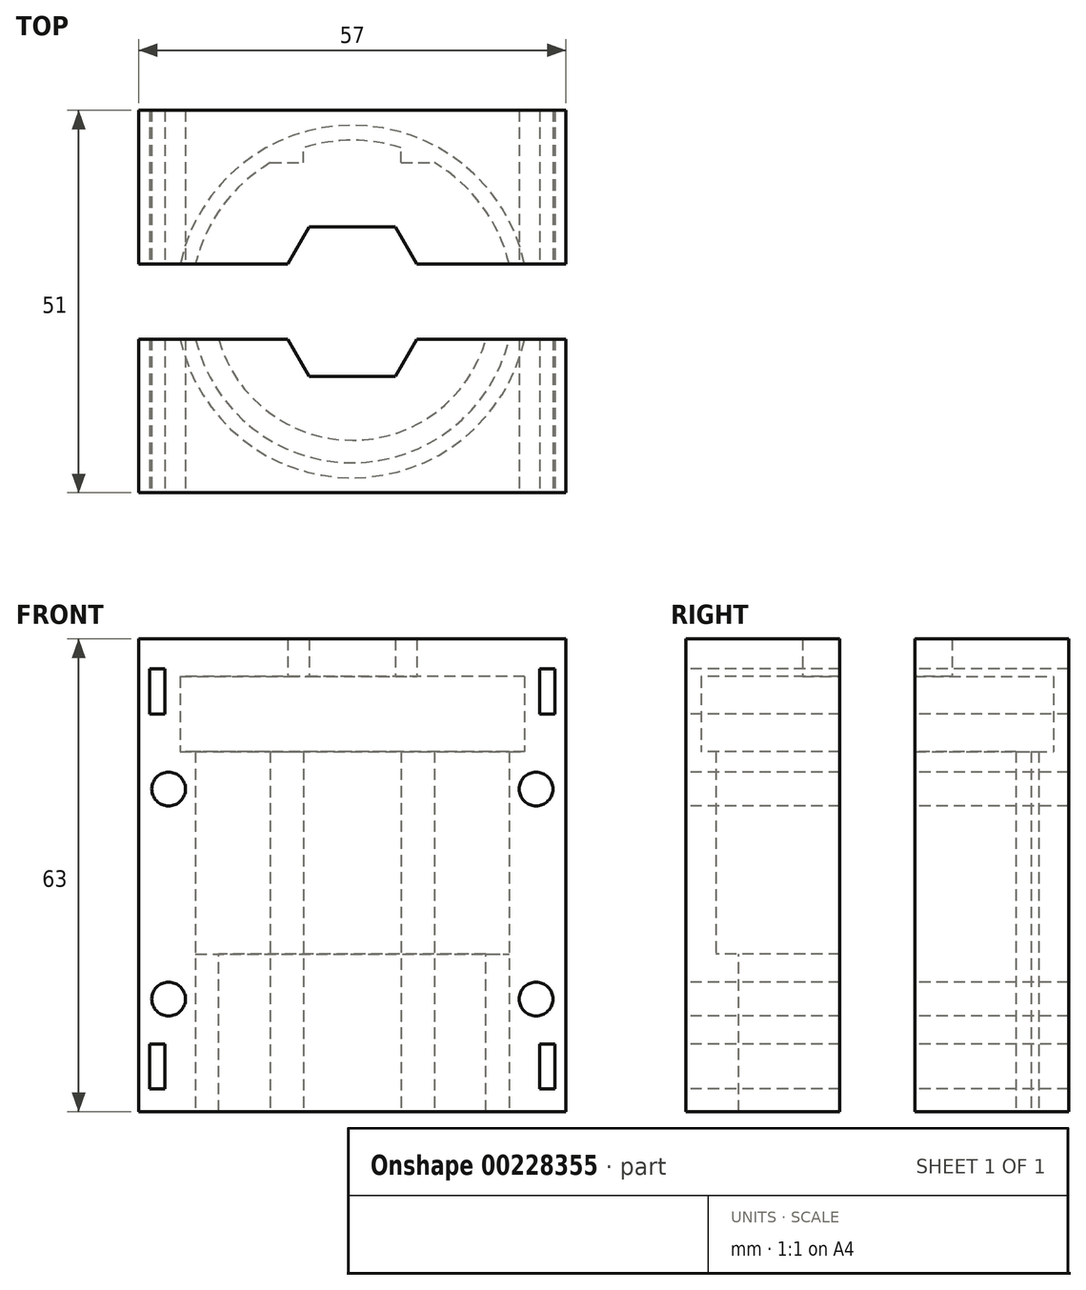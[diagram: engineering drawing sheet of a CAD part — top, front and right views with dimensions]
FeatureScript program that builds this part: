
annotation { "Feature Type Name" : "Feature", "Feature Type Description" : "" }
export const myFeature = defineFeature(function(context is Context, id is Id, definition is map)
    precondition{}
    {
        {
            var Q0;
            Q0=qCreatedBy(makeId("Top.planeOp"),FACE);
            var sketch = newSketch(context, id + "F0", { "sketchPlane" : qUnion([Q0])});
            skArc(sketch, "E0", {"start": v(-10.54, 17) * mm, "mid": v(0, -20) * mm, "end": v(10.54, 17) * mm, "construction": true});
            skLineSegment(sketch, "E1", {"start": v(0, 0) * mm, "end": v(0, 20) * mm, "construction": true});
            skLineSegment(sketch, "E2.0", {"start": v(5, 17) * mm, "end": v(5, 19.36) * mm, "construction": true});
            skLineSegment(sketch, "E3.0", {"start": v(-5, 17) * mm, "end": v(-5, 19.36) * mm, "construction": true});
            skLineSegment(sketch, "E4", {"start": v(-10.54, 17) * mm, "end": v(-5, 17) * mm, "construction": true});
            skLineSegment(sketch, "E5.trimOffspring", {"start": v(5, 17) * mm, "end": v(10.54, 17) * mm, "construction": true});
            skArc(sketch, "E6.trimOffspring", {"start": v(5, 19.36) * mm, "mid": v(0, 20) * mm, "end": v(-5, 19.36) * mm, "construction": true});
            skLineSegment(sketch, "E7.0", {"start": v(6.5, 18.5) * mm, "end": v(6.5, 20.5) * mm});
            skLineSegment(sketch, "E7.1", {"start": v(-6.5, 18.5) * mm, "end": v(-6.5, 20.5) * mm});
            skLineSegment(sketch, "E7.2", {"start": v(-10.95, 18.5) * mm, "end": v(-6.5, 18.5) * mm});
            skArc(sketch, "E7.3", {"start": v(6.5, 20.5) * mm, "mid": v(0, 21.5) * mm, "end": v(-6.5, 20.5) * mm});
            skArc(sketch, "E7.4", {"start": v(-10.95, 18.5) * mm, "mid": v(-18.68, 10.65) * mm, "end": v(-21.5, 0) * mm});
            skLineSegment(sketch, "E7.5", {"start": v(6.5, 18.5) * mm, "end": v(10.95, 18.5) * mm});
            skLineSegment(sketch, "E8", {"start": v(-21.5, 0) * mm, "end": v(21.5, 0) * mm, "construction": true});
            skLineSegment(sketch, "E9", {"start": v(-21.5, 21.5) * mm, "end": v(-21.5, -21.5) * mm, "construction": true});
            skLineSegment(sketch, "E10", {"start": v(21.5, 21.5) * mm, "end": v(21.5, -21.5) * mm, "construction": true});
            skLineSegment(sketch, "E11", {"start": v(-21.5, 21.5) * mm, "end": v(21.5, 21.5) * mm, "construction": true});
            skPoint(sketch, "E11.startSnap0", {"position": v(0, 21.5) * mm});
            skLineSegment(sketch, "E12", {"start": v(-21.5, -21.5) * mm, "end": v(21.5, -21.5) * mm, "construction": true});
            skPoint(sketch, "E12.startSnap0", {"position": v(0, -21.5) * mm});
            skLineSegment(sketch, "E13.0", {"start": v(-28.5, 25.5) * mm, "end": v(-28.5, 5) * mm});
            skLineSegment(sketch, "E14.0", {"start": v(28.5, 25.5) * mm, "end": v(28.5, 5) * mm});
            skLineSegment(sketch, "E15.0", {"start": v(-28.5, 25.5) * mm, "end": v(28.5, 25.5) * mm});
            skLineSegment(sketch, "E16.0", {"start": v(-28.5, -25.5) * mm, "end": v(28.5, -25.5) * mm});
            skLineSegment(sketch, "E17.0", {"start": v(-28.5, -5) * mm, "end": v(-20.91, -5) * mm});
            skLineSegment(sketch, "E18.0", {"start": v(-28.5, 5) * mm, "end": v(-20.91, 5) * mm});
            skLineSegment(sketch, "E19.trimOffspring", {"start": v(-28.5, -5) * mm, "end": v(-28.5, -25.5) * mm});
            skLineSegment(sketch, "E20.trimOffspring", {"start": v(28.5, -5) * mm, "end": v(28.5, -25.5) * mm});
            skArc(sketch, "E21.trimOffspring", {"start": v(20.91, 5) * mm, "mid": v(17.3, 12.76) * mm, "end": v(10.95, 18.5) * mm});
            skArc(sketch, "E22.trimOffspring", {"start": v(-20.91, -5) * mm, "mid": v(0, -21.5) * mm, "end": v(20.91, -5) * mm});
            skLineSegment(sketch, "E23.trimOffspring", {"start": v(20.91, -5) * mm, "end": v(28.5, -5) * mm});
            skLineSegment(sketch, "E24.trimOffspring", {"start": v(20.91, 5) * mm, "end": v(28.5, 5) * mm});
            skSolve(sketch);
        }
        {
            var Q0;
            Q0=makeQuery(id+"F0.imprint","IMPRINT",FACE,{"disambiguationData":[TD([[makeQuery(id+"F0.imprint","IMPRINT",EDGE,{"derivedFrom":sQuery(id+"F0.wireOp",EDGE,"E7.0")}),-1.0]])]});
            var Q1;
            Q1=makeQuery(id+"F0.imprint","IMPRINT",FACE,{"disambiguationData":[TD([[makeQuery(id+"F0.imprint","IMPRINT",EDGE,{"derivedFrom":sQuery(id+"F0.wireOp",EDGE,"E16.0")}),1.0]])]});
            extrude(context, id + "F1", {"entities" : qUnion([Q0, Q1]), "depth" : 27 * mm});
        }
        {
            var Q0;
            Q0=makeQuery(id+"F1.opExtrude","CAP_FACE",FACE,{"disambiguationData":[OSD([sQuery(id+"F0.wireOp",EDGE,"E7.0"),sQuery(id+"F0.wireOp",EDGE,"E7.1"),sQuery(id+"F0.wireOp",EDGE,"E7.2"),sQuery(id+"F0.wireOp",EDGE,"E7.3"),sQuery(id+"F0.wireOp",EDGE,"E7.4"),sQuery(id+"F0.wireOp",EDGE,"E7.5"),sQuery(id+"F0.wireOp",EDGE,"E13.0"),sQuery(id+"F0.wireOp",EDGE,"E14.0"),sQuery(id+"F0.wireOp",EDGE,"E15.0"),sQuery(id+"F0.wireOp",EDGE,"E18.0"),sQuery(id+"F0.wireOp",EDGE,"E21.trimOffspring"),sQuery(id+"F0.wireOp",EDGE,"E24.trimOffspring")])],"isStart":false});
            var sketch = newSketch(context, id + "F2", { "sketchPlane" : qUnion([Q0])});
            skLineSegment(sketch, "E25.0.0", {"start": v(28.5, 25.5) * mm, "end": v(-28.5, 25.5) * mm});
            skLineSegment(sketch, "E25.0.1", {"start": v(-28.5, 25.5) * mm, "end": v(-28.5, 5) * mm});
            skLineSegment(sketch, "E25.0.2", {"start": v(-28.5, 5) * mm, "end": v(-22.96, 5) * mm});
            skArc(sketch, "E25.0.3", {"start": v(-20.91, 5) * mm, "mid": v(-17.3, 12.76) * mm, "end": v(-10.95, 18.5) * mm, "construction": true});
            skLineSegment(sketch, "E25.0.4", {"start": v(-10.95, 18.5) * mm, "end": v(-6.5, 18.5) * mm, "construction": true});
            skLineSegment(sketch, "E25.0.5", {"start": v(-6.5, 18.5) * mm, "end": v(-6.5, 20.5) * mm, "construction": true});
            skArc(sketch, "E25.0.6", {"start": v(-6.5, 20.5) * mm, "mid": v(0, 21.5) * mm, "end": v(6.5, 20.5) * mm, "construction": true});
            skLineSegment(sketch, "E25.0.7", {"start": v(6.5, 20.5) * mm, "end": v(6.5, 18.5) * mm, "construction": true});
            skLineSegment(sketch, "E25.0.8", {"start": v(6.5, 18.5) * mm, "end": v(10.95, 18.5) * mm, "construction": true});
            skArc(sketch, "E25.0.9", {"start": v(10.95, 18.5) * mm, "mid": v(17.3, 12.76) * mm, "end": v(20.91, 5) * mm, "construction": true});
            skLineSegment(sketch, "E25.0.10", {"start": v(20.91, 5) * mm, "end": v(22.96, 5) * mm, "construction": true});
            skLineSegment(sketch, "E25.0.11", {"start": v(28.5, 5) * mm, "end": v(28.5, 25.5) * mm});
            skArc(sketch, "E26.0.0", {"start": v(20.91, -5) * mm, "mid": v(0, -21.5) * mm, "end": v(-20.91, -5) * mm, "construction": true});
            skLineSegment(sketch, "E26.0.1", {"start": v(-20.91, -5) * mm, "end": v(-22.96, -5) * mm, "construction": true});
            skLineSegment(sketch, "E26.0.2", {"start": v(-28.5, -5) * mm, "end": v(-28.5, -25.5) * mm});
            skLineSegment(sketch, "E26.0.3", {"start": v(-28.5, -25.5) * mm, "end": v(28.5, -25.5) * mm});
            skLineSegment(sketch, "E26.0.4", {"start": v(28.5, -25.5) * mm, "end": v(28.5, -5) * mm});
            skLineSegment(sketch, "E26.0.5", {"start": v(28.5, -5) * mm, "end": v(22.96, -5) * mm});
            skArc(sketch, "E27.0", {"start": v(22.96, -5) * mm, "mid": v(0, -23.5) * mm, "end": v(-22.96, -5) * mm});
            skLineSegment(sketch, "E28", {"start": v(-22.96, -5) * mm, "end": v(-28.5, -5) * mm});
            skLineSegment(sketch, "E29", {"start": v(22.96, -5) * mm, "end": v(20.91, -5) * mm, "construction": true});
            skArc(sketch, "E30.0", {"start": v(-22.96, 5) * mm, "mid": v(0, 23.5) * mm, "end": v(22.96, 5) * mm});
            skLineSegment(sketch, "E31", {"start": v(-22.96, 5) * mm, "end": v(-20.91, 5) * mm, "construction": true});
            skLineSegment(sketch, "E32", {"start": v(22.96, 5) * mm, "end": v(28.5, 5) * mm});
            skSolve(sketch);
        }
        {
            var Q0;
            Q0=makeQuery(id+"F2.imprint","IMPRINT",FACE,{"disambiguationData":[TD([[makeQuery(id+"F2.imprint","IMPRINT",EDGE,{"derivedFrom":sQuery(id+"F2.wireOp",EDGE,"E25.0.0")}),-1.0]])]});
            extrude(context, id + "F3", {"entities" : qUnion([Q0]), "operationType" : NewBodyOperationType.ADD, "depth" : 10 * mm});
        }
        {
            var Q0;
            Q0=makeQuery(id+"F2.imprint","IMPRINT",FACE,{"disambiguationData":[TD([[makeQuery(id+"F2.imprint","IMPRINT",EDGE,{"derivedFrom":sQuery(id+"F2.wireOp",EDGE,"E26.0.2")}),1.0]])]});
            extrude(context, id + "F4", {"entities" : qUnion([Q0]), "operationType" : NewBodyOperationType.ADD, "depth" : 10 * mm});
        }
        {
            var Q0;
            Q0=makeQuery(id+"F3.opExtrude","CAP_FACE",FACE,{"disambiguationData":[OSD([sQuery(id+"F2.wireOp",EDGE,"E25.0.0"),sQuery(id+"F2.wireOp",EDGE,"E25.0.1"),sQuery(id+"F2.wireOp",EDGE,"E25.0.2"),sQuery(id+"F2.wireOp",EDGE,"E25.0.11"),sQuery(id+"F2.wireOp",EDGE,"E30.0"),sQuery(id+"F2.wireOp",EDGE,"E32")])],"isStart":false});
            var sketch = newSketch(context, id + "F5", { "sketchPlane" : qUnion([Q0])});
            skLineSegment(sketch, "E33.0.0", {"start": v(-28.5, 5) * mm, "end": v(-22.96, 5) * mm});
            skLineSegment(sketch, "E33.0.2", {"start": v(22.96, 5) * mm, "end": v(28.5, 5) * mm});
            skLineSegment(sketch, "E33.0.3", {"start": v(28.5, 5) * mm, "end": v(28.5, 25.5) * mm});
            skLineSegment(sketch, "E33.0.4", {"start": v(28.5, 25.5) * mm, "end": v(-28.5, 25.5) * mm});
            skLineSegment(sketch, "E33.0.5", {"start": v(-28.5, 25.5) * mm, "end": v(-28.5, 5) * mm});
            skLineSegment(sketch, "E34.0.1", {"start": v(-22.96, -5) * mm, "end": v(-28.5, -5) * mm});
            skLineSegment(sketch, "E34.0.2", {"start": v(-28.5, -5) * mm, "end": v(-28.5, -25.5) * mm});
            skLineSegment(sketch, "E34.0.3", {"start": v(-28.5, -25.5) * mm, "end": v(28.5, -25.5) * mm});
            skLineSegment(sketch, "E34.0.4", {"start": v(28.5, -25.5) * mm, "end": v(28.5, -5) * mm});
            skLineSegment(sketch, "E34.0.5", {"start": v(28.5, -5) * mm, "end": v(22.96, -5) * mm});
            skLineSegment(sketch, "E35", {"start": v(0, 0) * mm, "end": v(28.5, 0) * mm, "construction": true});
            skCircle(sketch, "E36.cCircle", {"center": v(0, 0) * mm, "radius": 11.5 * mm, "construction": true});
            skLineSegment(sketch, "E36.0", {"start": v(8.61, -5) * mm, "end": v(5.75, -9.96) * mm});
            skLineSegment(sketch, "E36.1", {"start": v(5.75, -9.96) * mm, "end": v(-5.75, -9.96) * mm});
            skLineSegment(sketch, "E36.2", {"start": v(-5.75, -9.96) * mm, "end": v(-8.61, -5) * mm});
            skLineSegment(sketch, "E36.3", {"start": v(-8.61, 5) * mm, "end": v(-5.75, 9.96) * mm});
            skLineSegment(sketch, "E36.4", {"start": v(-5.75, 9.96) * mm, "end": v(5.75, 9.96) * mm});
            skLineSegment(sketch, "E36.5", {"start": v(5.75, 9.96) * mm, "end": v(8.61, 5) * mm});
            skLineSegment(sketch, "E37", {"start": v(-22.96, 5) * mm, "end": v(-8.61, 5) * mm});
            skLineSegment(sketch, "E38", {"start": v(22.96, 5) * mm, "end": v(8.61, 5) * mm});
            skLineSegment(sketch, "E39", {"start": v(-22.96, -5) * mm, "end": v(-8.61, -5) * mm});
            skLineSegment(sketch, "E40", {"start": v(22.96, -5) * mm, "end": v(8.61, -5) * mm});
            skPoint(sketch, "E41.orphan", {"position": v(11.5, 0) * mm});
            skPoint(sketch, "E42.orphan", {"position": v(-11.5, 0) * mm});
            skSolve(sketch);
        }
        {
            var Q0;
            Q0=makeQuery(id+"F5.imprint","IMPRINT",FACE,{"disambiguationData":[TD([[makeQuery(id+"F5.imprint","IMPRINT",EDGE,{"derivedFrom":sQuery(id+"F5.wireOp",EDGE,"E36.3")}),1.0]])]});
            var Q1;
            Q1=makeQuery(id+"F5.imprint","IMPRINT",FACE,{"disambiguationData":[TD([[makeQuery(id+"F5.imprint","IMPRINT",EDGE,{"derivedFrom":sQuery(id+"F5.wireOp",EDGE,"E33.0.0")}),1.0]])]});
            extrude(context, id + "F6", {"entities" : qUnion([Q0, Q1]), "operationType" : NewBodyOperationType.ADD, "depth" : 5 * mm});
        }
        {
            var Q0;
            Q0=makeQuery(id+"F5.imprint","IMPRINT",FACE,{"disambiguationData":[TD([[makeQuery(id+"F5.imprint","IMPRINT",EDGE,{"derivedFrom":sQuery(id+"F5.wireOp",EDGE,"E34.0.1")}),1.0]])]});
            extrude(context, id + "F7", {"entities" : qUnion([Q0]), "operationType" : NewBodyOperationType.ADD, "depth" : 5 * mm});
        }
        {
            var Q0;
            Q0=makeQuery(id+"F1.opExtrude","CAP_FACE",FACE,{"disambiguationData":[OSD([sQuery(id+"F0.wireOp",EDGE,"E7.0"),sQuery(id+"F0.wireOp",EDGE,"E7.1"),sQuery(id+"F0.wireOp",EDGE,"E7.2"),sQuery(id+"F0.wireOp",EDGE,"E7.3"),sQuery(id+"F0.wireOp",EDGE,"E7.4"),sQuery(id+"F0.wireOp",EDGE,"E7.5"),sQuery(id+"F0.wireOp",EDGE,"E13.0"),sQuery(id+"F0.wireOp",EDGE,"E14.0"),sQuery(id+"F0.wireOp",EDGE,"E15.0"),sQuery(id+"F0.wireOp",EDGE,"E18.0"),sQuery(id+"F0.wireOp",EDGE,"E21.trimOffspring"),sQuery(id+"F0.wireOp",EDGE,"E24.trimOffspring")])],"isStart":true});
            var sketch = newSketch(context, id + "F8", { "sketchPlane" : qUnion([Q0])});
            skArc(sketch, "E43.0.0", {"start": v(-20.91, 5) * mm, "mid": v(0, 21.5) * mm, "end": v(20.91, 5) * mm, "construction": true});
            skLineSegment(sketch, "E43.0.1", {"start": v(20.91, 5) * mm, "end": v(28.5, 5) * mm});
            skLineSegment(sketch, "E43.0.2", {"start": v(28.5, 5) * mm, "end": v(28.5, 25.5) * mm});
            skLineSegment(sketch, "E43.0.3", {"start": v(28.5, 25.5) * mm, "end": v(-28.5, 25.5) * mm});
            skLineSegment(sketch, "E43.0.4", {"start": v(-28.5, 25.5) * mm, "end": v(-28.5, 5) * mm});
            skLineSegment(sketch, "E43.0.5", {"start": v(-28.5, 5) * mm, "end": v(-20.91, 5) * mm});
            skLineSegment(sketch, "E44.0.0", {"start": v(-28.5, -25.5) * mm, "end": v(28.5, -25.5) * mm});
            skLineSegment(sketch, "E44.0.1", {"start": v(28.5, -25.5) * mm, "end": v(28.5, -5) * mm});
            skLineSegment(sketch, "E44.0.2", {"start": v(28.5, -5) * mm, "end": v(20.91, -5) * mm});
            skArc(sketch, "E44.0.3", {"start": v(20.91, -5) * mm, "mid": v(17.3, -12.76) * mm, "end": v(10.95, -18.5) * mm, "construction": true});
            skLineSegment(sketch, "E44.0.4", {"start": v(10.95, -18.5) * mm, "end": v(6.5, -18.5) * mm, "construction": true});
            skLineSegment(sketch, "E44.0.5", {"start": v(6.5, -18.5) * mm, "end": v(6.5, -20.5) * mm, "construction": true});
            skArc(sketch, "E44.0.6", {"start": v(6.5, -20.5) * mm, "mid": v(0, -21.5) * mm, "end": v(-6.5, -20.5) * mm, "construction": true});
            skLineSegment(sketch, "E44.0.7", {"start": v(-6.5, -20.5) * mm, "end": v(-6.5, -18.5) * mm, "construction": true});
            skLineSegment(sketch, "E44.0.8", {"start": v(-6.5, -18.5) * mm, "end": v(-10.95, -18.5) * mm, "construction": true});
            skArc(sketch, "E44.0.9", {"start": v(-10.95, -18.5) * mm, "mid": v(-17.3, -12.76) * mm, "end": v(-20.91, -5) * mm, "construction": true});
            skLineSegment(sketch, "E44.0.10", {"start": v(-20.91, -5) * mm, "end": v(-28.5, -5) * mm});
            skLineSegment(sketch, "E44.0.11", {"start": v(-28.5, -5) * mm, "end": v(-28.5, -25.5) * mm});
            skArc(sketch, "E45.0", {"start": v(-17.81, 5) * mm, "mid": v(0, 18.5) * mm, "end": v(17.81, 5) * mm});
            skArc(sketch, "E46.0", {"start": v(17.81, -5) * mm, "mid": v(0, -18.5) * mm, "end": v(-17.81, -5) * mm});
            skLineSegment(sketch, "E47", {"start": v(-20.91, 5) * mm, "end": v(-17.81, 5) * mm});
            skLineSegment(sketch, "E48", {"start": v(17.81, 5) * mm, "end": v(20.91, 5) * mm});
            skLineSegment(sketch, "E49", {"start": v(20.91, -5) * mm, "end": v(17.81, -5) * mm});
            skLineSegment(sketch, "E50", {"start": v(-17.81, -5) * mm, "end": v(-20.91, -5) * mm});
            skSolve(sketch);
        }
        {
            var Q0;
            Q0=makeQuery(id+"F8.imprint","IMPRINT",FACE,{"disambiguationData":[TD([[makeQuery(id+"F8.imprint","IMPRINT",EDGE,{"derivedFrom":sQuery(id+"F8.wireOp",EDGE,"E43.0.1")}),1.0]])]});
            extrude(context, id + "F9", {"entities" : qUnion([Q0]), "operationType" : NewBodyOperationType.ADD, "depth" : 21 * mm});
        }
        {
            var Q0;
            Q0=makeQuery(id+"F8.imprint","IMPRINT",FACE,{"disambiguationData":[TD([[makeQuery(id+"F8.imprint","IMPRINT",EDGE,{"derivedFrom":sQuery(id+"F8.wireOp",EDGE,"E46.0")}),1.0]])]});
            var Q1;
            Q1=makeQuery(id+"F8.imprint","IMPRINT",FACE,{"disambiguationData":[TD([[makeQuery(id+"F8.imprint","IMPRINT",EDGE,{"derivedFrom":sQuery(id+"F8.wireOp",EDGE,"E44.0.0")}),1.0]])]});
            extrude(context, id + "F10", {"entities" : qUnion([Q0, Q1]), "operationType" : NewBodyOperationType.ADD, "depth" : 21 * mm});
        }
        {
            var Q0;
            Q0=makeQuery(id+"F9.boolean.opBoolean","MERGE",FACE,{"derivedFrom":[makeQuery(id+"F7.boolean.opBoolean","MERGE",FACE,{"derivedFrom":[makeQuery(id+"F4.boolean.opBoolean","MERGE",FACE,{"derivedFrom":[makeQuery(id+"F1.opExtrude","SWEPT_FACE",FACE,{"disambiguationData":[OSD([sQuery(id+"F0.wireOp",EDGE,"E16.0")])]}),makeQuery(id+"F4.opExtrude","SWEPT_FACE",FACE,{"disambiguationData":[OSD([sQuery(id+"F2.wireOp",EDGE,"E26.0.3")])]})]}),makeQuery(id+"F7.opExtrude","SWEPT_FACE",FACE,{"disambiguationData":[OSD([sQuery(id+"F5.wireOp",EDGE,"E34.0.3")])]})]}),makeQuery(id+"F9.opExtrude","SWEPT_FACE",FACE,{"disambiguationData":[OSD([sQuery(id+"F8.wireOp",EDGE,"E43.0.3")])]})]});
            var sketch = newSketch(context, id + "F11", { "sketchPlane" : qUnion([Q0])});
            skLineSegment(sketch, "E51.0.0", {"start": v(-28.5, 42) * mm, "end": v(-28.5, -21) * mm, "construction": true});
            skLineSegment(sketch, "E51.0.1", {"start": v(-28.5, -21) * mm, "end": v(28.5, -21) * mm, "construction": true});
            skLineSegment(sketch, "E51.0.2", {"start": v(28.5, -21) * mm, "end": v(28.5, 42) * mm, "construction": true});
            skLineSegment(sketch, "E51.0.3", {"start": v(28.5, 42) * mm, "end": v(-28.5, 42) * mm, "construction": true});
            skPoint(sketch, "E52", {"position": v(-24.5, 22) * mm});
            skPoint(sketch, "E53", {"position": v(24.5, 22) * mm});
            skPoint(sketch, "E54", {"position": v(24.5, -6) * mm});
            skPoint(sketch, "E55", {"position": v(-24.5, -6) * mm});
            skLineSegment(sketch, "E56.bottom", {"start": v(-25, 38) * mm, "end": v(-27, 38) * mm});
            skLineSegment(sketch, "E56.top", {"start": v(-25, 32) * mm, "end": v(-27, 32) * mm});
            skLineSegment(sketch, "E56.left", {"start": v(-25, 38) * mm, "end": v(-25, 32) * mm});
            skLineSegment(sketch, "E56.right", {"start": v(-27, 38) * mm, "end": v(-27, 32) * mm});
            skLineSegment(sketch, "E57.bottom", {"start": v(25, 38) * mm, "end": v(27, 38) * mm});
            skLineSegment(sketch, "E57.top", {"start": v(25, 32) * mm, "end": v(27, 32) * mm});
            skLineSegment(sketch, "E57.left", {"start": v(25, 38) * mm, "end": v(25, 32) * mm});
            skLineSegment(sketch, "E57.right", {"start": v(27, 38) * mm, "end": v(27, 32) * mm});
            skLineSegment(sketch, "E58.bottom", {"start": v(-27, -12) * mm, "end": v(-25, -12) * mm});
            skLineSegment(sketch, "E58.top", {"start": v(-27, -18) * mm, "end": v(-25, -18) * mm});
            skLineSegment(sketch, "E58.left", {"start": v(-27, -12) * mm, "end": v(-27, -18) * mm});
            skLineSegment(sketch, "E58.right", {"start": v(-25, -12) * mm, "end": v(-25, -18) * mm});
            skLineSegment(sketch, "E59.bottom", {"start": v(27, -18) * mm, "end": v(25, -18) * mm});
            skLineSegment(sketch, "E59.top", {"start": v(27, -12) * mm, "end": v(25, -12) * mm});
            skLineSegment(sketch, "E59.left", {"start": v(27, -18) * mm, "end": v(27, -12) * mm});
            skLineSegment(sketch, "E59.right", {"start": v(25, -18) * mm, "end": v(25, -12) * mm});
            skSolve(sketch);
        }
        {
            var Q0;
            Q0=sQuery(id+"F11.wireOp",VERTEX,"E53");
            var Q1;
            Q1=sQuery(id+"F11.wireOp",VERTEX,"E54");
            var Q2;
            Q2=sQuery(id+"F11.wireOp",VERTEX,"E52");
            var Q3;
            Q3=sQuery(id+"F11.wireOp",VERTEX,"E55");
            var Q4;
            Q4=makeQuery(id+"F1.opExtrude","SWEPT_BODY",BODY,{"disambiguationData":[OSD([sQuery(id+"F0.wireOp",EDGE,"E7.0"),sQuery(id+"F0.wireOp",EDGE,"E7.1"),sQuery(id+"F0.wireOp",EDGE,"E7.2"),sQuery(id+"F0.wireOp",EDGE,"E7.3"),sQuery(id+"F0.wireOp",EDGE,"E7.4"),sQuery(id+"F0.wireOp",EDGE,"E7.5"),sQuery(id+"F0.wireOp",EDGE,"E13.0"),sQuery(id+"F0.wireOp",EDGE,"E14.0"),sQuery(id+"F0.wireOp",EDGE,"E15.0"),sQuery(id+"F0.wireOp",EDGE,"E18.0"),sQuery(id+"F0.wireOp",EDGE,"E21.trimOffspring"),sQuery(id+"F0.wireOp",EDGE,"E24.trimOffspring")])]});
            var Q5;
            Q5=makeQuery(id+"F1.opExtrude","SWEPT_BODY",BODY,{"disambiguationData":[OSD([sQuery(id+"F0.wireOp",EDGE,"E16.0"),sQuery(id+"F0.wireOp",EDGE,"E17.0"),sQuery(id+"F0.wireOp",EDGE,"E19.trimOffspring"),sQuery(id+"F0.wireOp",EDGE,"E20.trimOffspring"),sQuery(id+"F0.wireOp",EDGE,"E22.trimOffspring"),sQuery(id+"F0.wireOp",EDGE,"E23.trimOffspring")])]});
            hole(context, id + "F12", {"style" : HoleStyle.SIMPLE, "endStyle" : HoleEndStyle.THROUGH, "holeDiameter" : 4.5 * mm, "locations" : qUnion([Q0, Q1, Q2, Q3]), "scope" : qUnion([Q4, Q5]), "isTappedThrough" : true});
        }
        {
            var Q0;
            Q0 = qSketchRegion(id + "F11", true);
            extrude(context, id + "F13", {"entities" : qUnion([Q0]), "operationType" : NewBodyOperationType.REMOVE, "endBound" : BoundingType.THROUGH_ALL, "oppositeDirection" : true, "depth" : 25 * mm});
        }
    });
